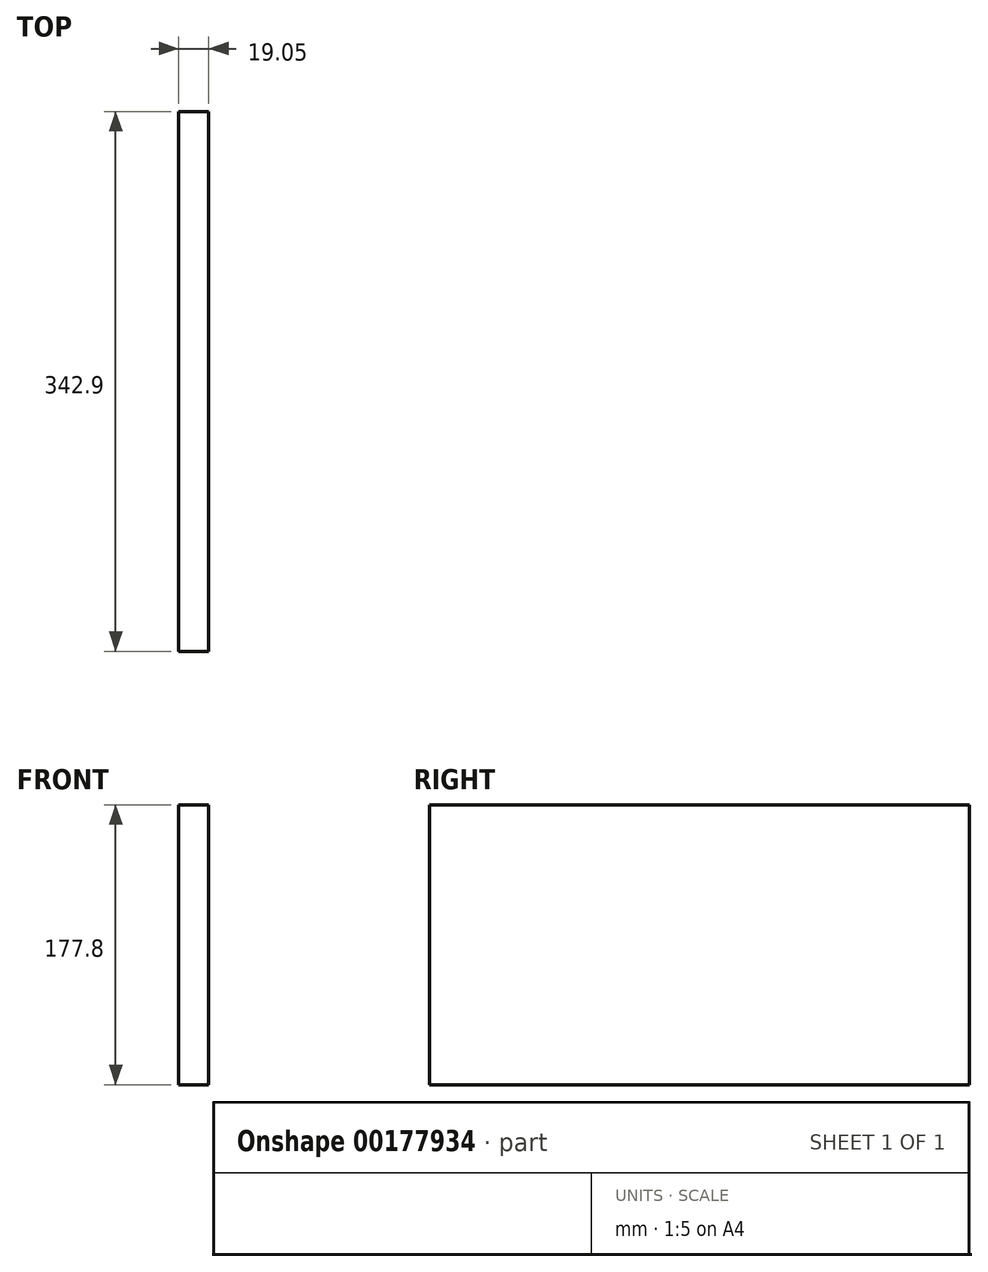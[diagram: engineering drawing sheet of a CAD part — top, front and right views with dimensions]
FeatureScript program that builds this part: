
annotation { "Feature Type Name" : "Feature", "Feature Type Description" : "" }
export const myFeature = defineFeature(function(context is Context, id is Id, definition is map)
    precondition{}
    {
        {
            var Q0;
            Q0=qCreatedBy(makeId("Right.planeOp"),FACE);
            var sketch = newSketch(context, id + "F0", { "sketchPlane" : qUnion([Q0])});
            skLineSegment(sketch, "E0.bottom", {"start": v(0, 0) * mm, "end": v(342.9, 0) * mm});
            skLineSegment(sketch, "E0.top", {"start": v(0, 177.8) * mm, "end": v(342.9, 177.8) * mm});
            skLineSegment(sketch, "E0.left", {"start": v(0, 0) * mm, "end": v(0, 177.8) * mm});
            skLineSegment(sketch, "E0.right", {"start": v(342.9, 0) * mm, "end": v(342.9, 177.8) * mm});
            skSolve(sketch);
        }
        {
            var Q0;
            Q0=makeQuery(id+"F0.imprint","IMPRINT",FACE,{"disambiguationData":[TD([[makeQuery(id+"F0.imprint","IMPRINT",EDGE,{"derivedFrom":sQuery(id+"F0.wireOp",EDGE,"E0.bottom")}),1.0]])]});
            extrude(context, id + "F1", {"entities" : qUnion([Q0]), "depth" : 19.05 * mm});
        }
    });
